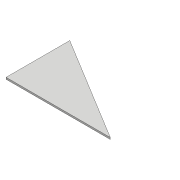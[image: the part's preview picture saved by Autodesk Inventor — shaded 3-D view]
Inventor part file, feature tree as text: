
AUTODESK INVENTOR PART (.ipt)
format: ipt  version: 2017 (Build 210142000, 142)  size: 69,632 bytes
history: native  units: mm
features: extrude x1, sketch x1
ambient origin geometry x8: Origin, YZ Plane, XZ Plane, XY Plane, X Axis, Y Axis, Z Axis, Center Point
bodies: Solid1 (feature_tree)
feature tree (2):
  extrude  "Extrusion1"  Depth=10.0mm
  sketch  "Sketch1"  dims[d0=365.0mm d1=700.0mm d2=10.0mm d3=0.0mm]
